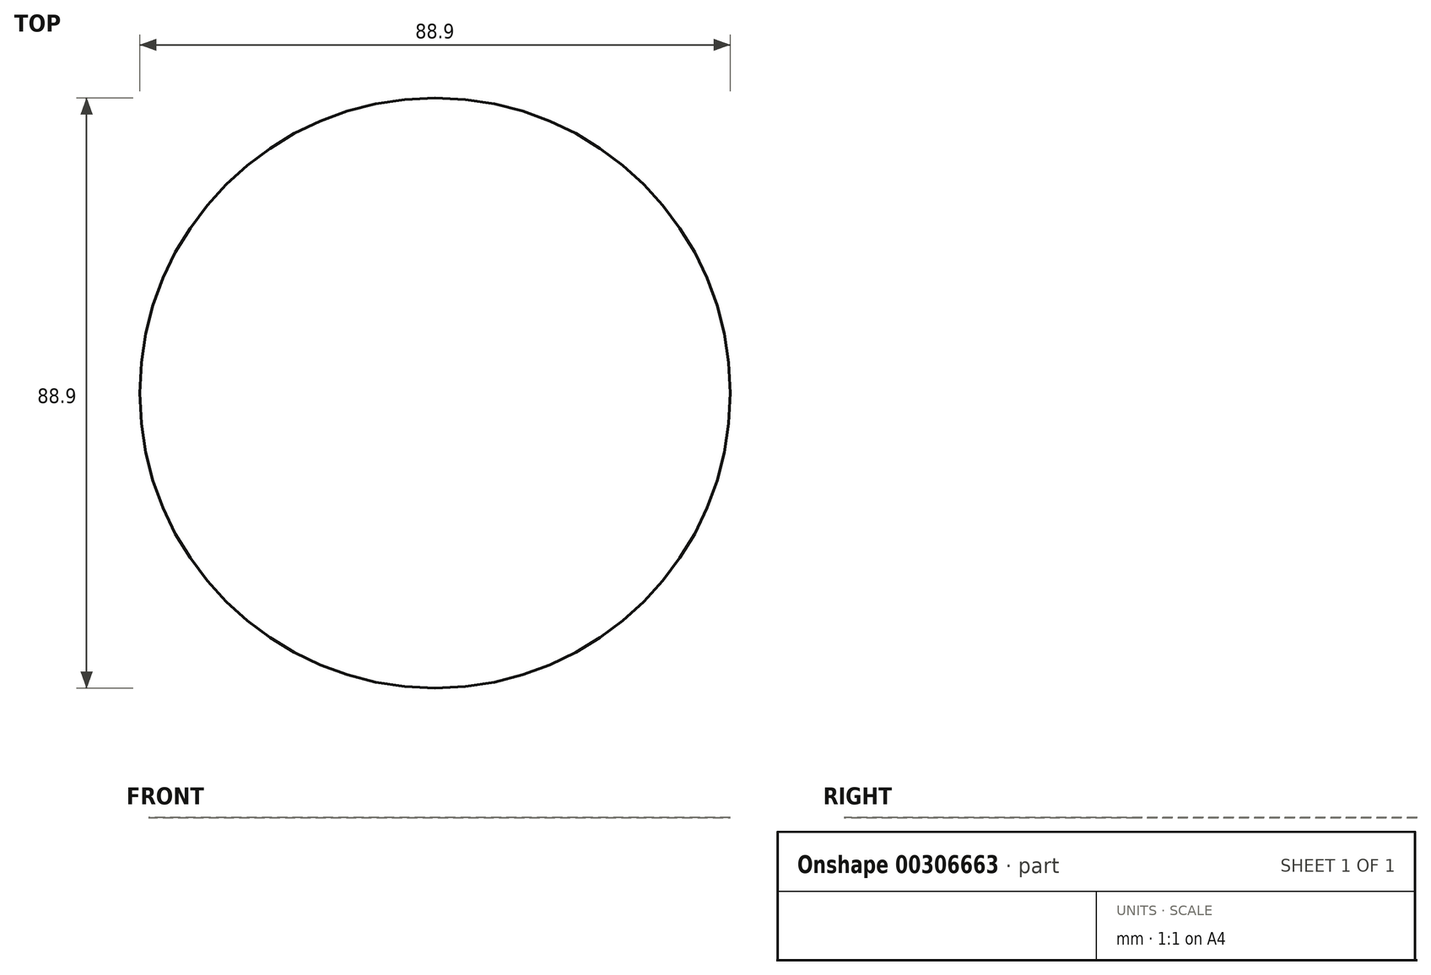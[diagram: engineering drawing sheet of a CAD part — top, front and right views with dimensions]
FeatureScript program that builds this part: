
annotation { "Feature Type Name" : "Feature", "Feature Type Description" : "" }
export const myFeature = defineFeature(function(context is Context, id is Id, definition is map)
    precondition{}
    {
        {
            var Q0;
            Q0=qCreatedBy(makeId("Front.planeOp"),FACE);
            var sketch = newSketch(context, id + "F0", { "sketchPlane" : qUnion([Q0])});
            skLineSegment(sketch, "E0", {"start": v(0, 76.99) * mm, "end": v(0, 0) * mm, "construction": true});
            skLineSegment(sketch, "E1", {"start": v(-44.45, 0) * mm, "end": v(0, 0) * mm, "construction": true});
            skArc(sketch, "E2", {"start": v(-44.45, 0) * mm, "mid": v(-11.91, 32.54) * mm, "end": v(0, 76.99) * mm});
            skLineSegment(sketch, "E3", {"start": v(0, 76.99) * mm, "end": v(0, 0) * mm});
            skLineSegment(sketch, "E4", {"start": v(0, 0) * mm, "end": v(-44.45, 0) * mm});
            skSolve(sketch);
        }
        {
            var Q0;
            Q0=makeQuery(id+"F0.imprint","IMPRINT",FACE,{"disambiguationData":[TD([[makeQuery(id+"F0.imprint","IMPRINT",EDGE,{"derivedFrom":sQuery(id+"F0.wireOp",EDGE,"E2")}),-1.0]])]});
            var Q1;
            Q1=sQuery(id+"F0.wireOp",EDGE,"E3");
            revolve(context, id + "F1", {"entities" : qUnion([Q0]), "axis" : qUnion([Q1]), "revolveType" : RevolveType.FULL});
        }
    });
